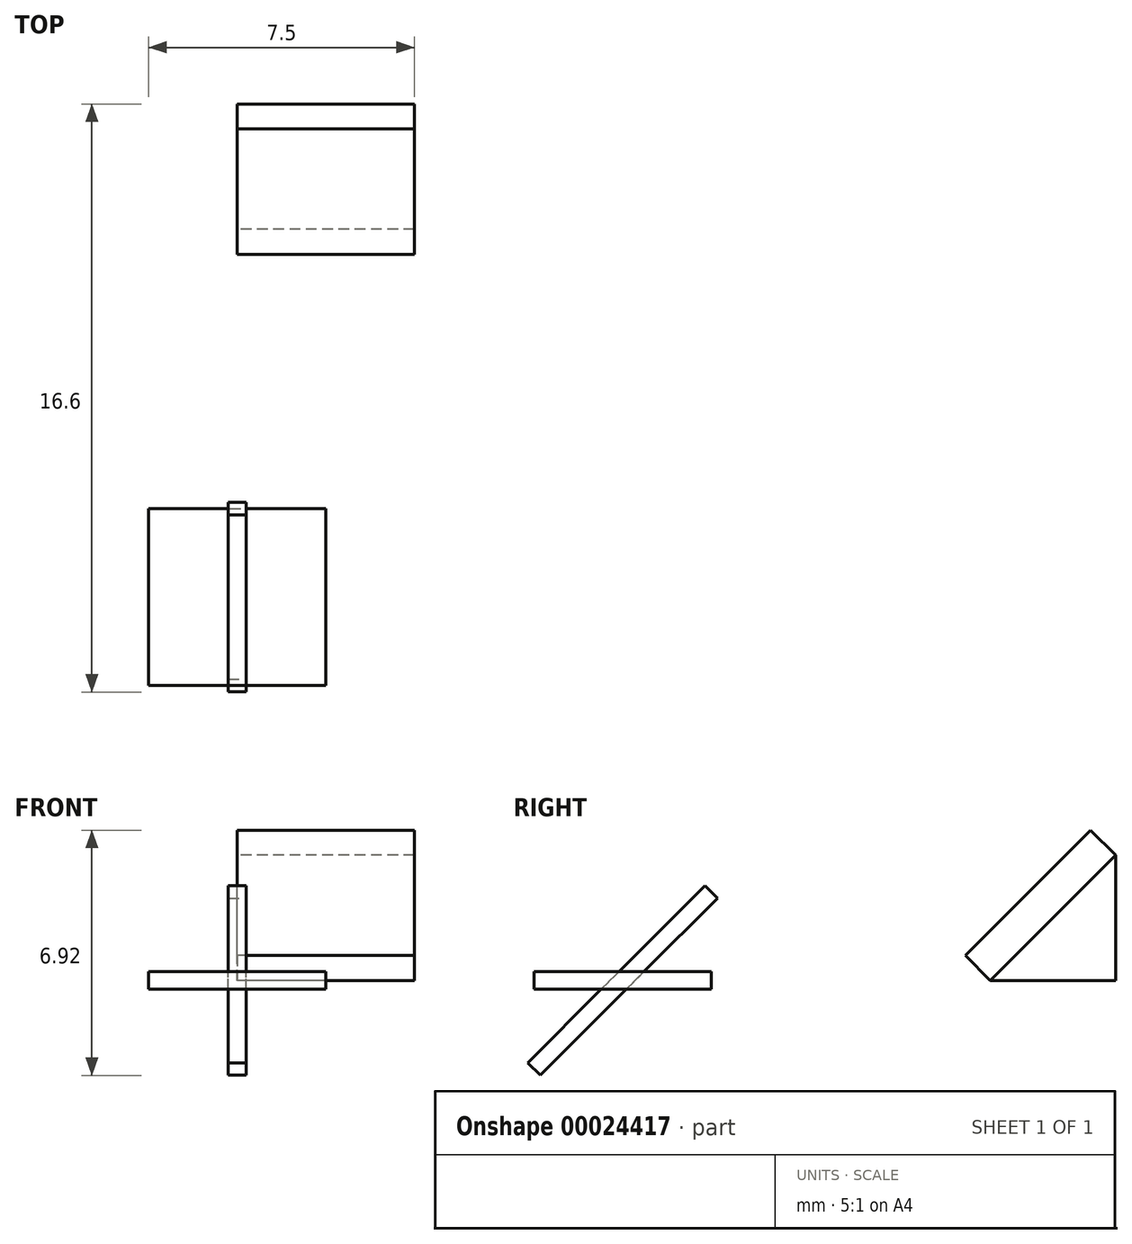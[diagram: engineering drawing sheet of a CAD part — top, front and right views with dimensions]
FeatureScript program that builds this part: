
annotation { "Feature Type Name" : "Feature", "Feature Type Description" : "" }
export const myFeature = defineFeature(function(context is Context, id is Id, definition is map)
    precondition{}
    {
        {
            var Q0;
            Q0=qCreatedBy(makeId("Right.planeOp"),FACE);
            var sketch = newSketch(context, id + "F0", { "sketchPlane" : qUnion([Q0])});
            skLineSegment(sketch, "E0", {"start": v(0, 0) * mm, "end": v(-3.54, 0) * mm});
            skLineSegment(sketch, "E1", {"start": v(-3.54, 0) * mm, "end": v(0, 3.54) * mm});
            skLineSegment(sketch, "E2", {"start": v(0, 3.54) * mm, "end": v(0, 0) * mm});
            skSolve(sketch);
        }
        {
            var Q0;
            Q0=makeQuery(id+"F0.imprint","IMPRINT",FACE,{"disambiguationData":[TD([[makeQuery(id+"F0.imprint","IMPRINT",EDGE,{"derivedFrom":sQuery(id+"F0.wireOp",EDGE,"E0")}),-1.0]])]});
            extrude(context, id + "F6", {"entities" : qUnion([Q0]), "depth" : 5 * mm});
        }
        {
            var Q0;
            Q0=makeQuery(id+"F6.opExtrude","SWEPT_FACE",FACE,{"disambiguationData":[OSD([sQuery(id+"F0.wireOp",EDGE,"E1")])]});
            extrude(context, id + "F7", {"entities" : qUnion([Q0]), "depth" : 1 * mm});
        }
        {
            var Q0;
            Q0=qCreatedBy(makeId("Top.planeOp"),FACE);
            var sketch = newSketch(context, id + "F1", { "sketchPlane" : qUnion([Q0])});
            skLineSegment(sketch, "E3.rect.bottom", {"start": v(-2.5, -11.42) * mm, "end": v(2.5, -11.42) * mm});
            skLineSegment(sketch, "E3.rect.top", {"start": v(-2.5, -16.42) * mm, "end": v(2.5, -16.42) * mm});
            skLineSegment(sketch, "E3.rect.left", {"start": v(-2.5, -11.42) * mm, "end": v(-2.5, -16.42) * mm});
            skLineSegment(sketch, "E3.rect.right", {"start": v(2.5, -11.42) * mm, "end": v(2.5, -16.42) * mm});
            skPoint(sketch, "E3.rect.middle", {"position": v(0, -13.92) * mm});
            skSolve(sketch);
        }
        {
            var Q0;
            Q0=qCreatedBy(makeId("Right.planeOp"),FACE);
            var sketch = newSketch(context, id + "F2", { "sketchPlane" : qUnion([Q0])});
            skPoint(sketch, "E4.rect.middle", {"position": v(-13.92, 0) * mm});
            skLineSegment(sketch, "E5", {"start": v(-16.42, -2.5) * mm, "end": v(-11.42, 2.5) * mm});
            skSolve(sketch);
        }
        {
            var Q0;
            Q0 = qSketchRegion(id + "F2", true);
            var Q1;
            Q1=makeQuery(id+"F1.imprint","IMPRINT",FACE,{"disambiguationData":[TD([[makeQuery(id+"F1.imprint","IMPRINT",EDGE,{"derivedFrom":sQuery(id+"F1.wireOp",EDGE,"E3.rect.bottom")}),-1.0]])]});
            extrude(context, id + "F3", {"entities" : qUnion([Q0, Q1]), "endBound" : BoundingType.SYMMETRIC, "depth" : .5 * mm});
        }
        {
            var Q0;
            Q0=sQuery(id+"F2.wireOp",EDGE,"E5");
            extrude(context, id + "F4", {"bodyType" : ToolBodyType.SURFACE, "surfaceEntities" : qUnion([Q0]), "endBound" : BoundingType.SYMMETRIC, "depth" : .5 * mm});
        }
        {
            var Q0;
            Q0=makeQuery(id+"F4.opExtrude","SWEPT_FACE",FACE,{"disambiguationData":[OSD([sQuery(id+"F2.wireOp",EDGE,"E5")])]});
            extrude(context, id + "F5", {"entities" : qUnion([Q0]), "endBound" : BoundingType.SYMMETRIC, "depth" : .5 * mm});
        }
    });
